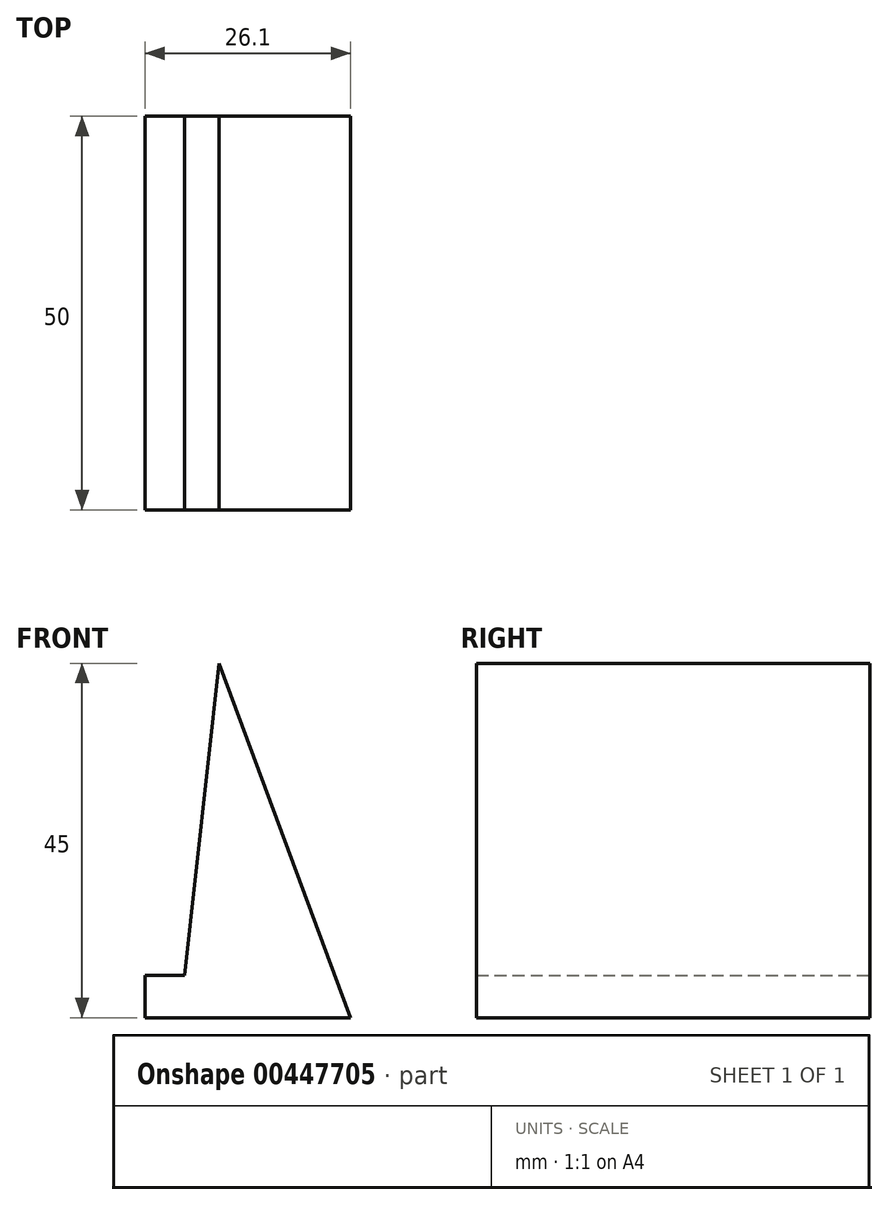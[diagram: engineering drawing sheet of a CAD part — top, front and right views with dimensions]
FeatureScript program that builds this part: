
annotation { "Feature Type Name" : "Feature", "Feature Type Description" : "" }
export const myFeature = defineFeature(function(context is Context, id is Id, definition is map)
    precondition{}
    {
        {
            var Q0;
            Q0=qCreatedBy(makeId("Front.planeOp"),FACE);
            var sketch = newSketch(context, id + "F0", { "sketchPlane" : qUnion([Q0])});
            skLineSegment(sketch, "E0", {"start": v(-12.18, -33.08) * mm, "end": v(8.92, -33.08) * mm});
            skLineSegment(sketch, "E1", {"start": v(-12.18, -27.7) * mm, "end": v(-17.18, -27.7) * mm});
            skLineSegment(sketch, "E2", {"start": v(-12.18, -33.08) * mm, "end": v(-17.18, -33.08) * mm});
            skLineSegment(sketch, "E3", {"start": v(-17.18, -27.7) * mm, "end": v(-17.18, -33.08) * mm});
            skLineSegment(sketch, "E4", {"start": v(-12.18, -27.7) * mm, "end": v(-7.8, 11.92) * mm});
            skLineSegment(sketch, "E5", {"start": v(-7.8, 11.92) * mm, "end": v(8.92, -33.08) * mm});
            skLineSegment(sketch, "E6", {"start": v(-12.18, -33.08) * mm, "end": v(-12.18, 11.92) * mm, "construction": true});
            skSolve(sketch);
        }
        {
            var Q0;
            Q0 = qSketchRegion(id + "F0", true);
            extrude(context, id + "F1", {"entities" : qUnion([Q0]), "depth" : 50 * mm});
        }
    });
